# Revit family: gooo__55_eb_led_2w_350-700ma__2700k_160lm__cri90_220-0427_7cab
name_source: partatom
category: Lighting Fixtures
units: mm (PartAtom-declared; Revit-internal decimal feet)

## family parameters
Cut with Voids When Loaded = No
Host = Face
Light Source = No
Part Type = Normal
Room Calculation Point = No
Round Connector Dimension = Use Diameter
Shared = No

## types (1)
- 220-0427- (1 x LED, 160 lm, 2.3 W, 2700K)
    Apparent Load = 2 VA
    CIE Flux Codes = 12 40 70 99 28
    Color Rendering = 1A/90…99
    Color Temperature = 2700K
    Default Elevation = 1800 mm
    Description = The recessed luminaire GOOO! from the familiy DELIGHT consists of aluminum. Stated photometric values correspond to operation by 700 mA; a suitable ballast needs to be sourced separately and is not scope of delivery. Dimming (# 220-0427) depends on the used ballast and may vary. The asymmetric Wallwash luminaire corresponds to protection class SK3 at IP20.
    Height = 0 mm  [stored 0 ft]
    Lamp = 1 x LED
    Lamp Light Flux = 160 lm
    Lamp Power = 2.3 W
    Lamp count = 1
    Length = 55 mm
    Luminous efficacy = 20 lm/W
    Manufacturer = Prolicht
    ModVariant = No
    Model = 220-0427
    Mounting Place = Ceiling
    Mounting Type = Recessed
    Number of Poles = 1
    OnlyDefault = Yes
    Power Factor = 1
    Product Name = GOOO! 55 EB LED 2W 350-700mA  2700K 160lm  CRI90
    Product group = Recessed lights
    ProductGroupID = 421
    Protection Class = Protection class
    Protection Degree = Degree of protection
    RLX_Detail_Level = 1
    RLX_Emergency_Light_Flux = 0 lm
    RLX_Emergency_Type = 0
    RLX_Emergency_Type_DB = No
    Recessed Depth = -60 mm
    Recessed Length = 48 mm  [stored 0.15748 ft]
    Recessed Width = 48 mm  [stored 0.15748 ft]
    RlxData = <blob elided: 72061 chars, md5=cfc2d7e9>
    Socket = socket
    Standby Power = 0 W
    System Light Flux = 46 lm
    System Power = 2 W
    Type Image = 220-0427.jpg
    URL = http://relux.com
    VarID = 220-0427-
    Voltage = 0 V
    Weight = 0.00 kg
    Width = 55 mm

note: [stored X ft] marks values corroborated as IEEE doubles in the binary element streams (Revit-internal decimal feet)

## geometry (parser evidence)
native form markers: Sweep x10
no freeform markers — native parametric forms only
